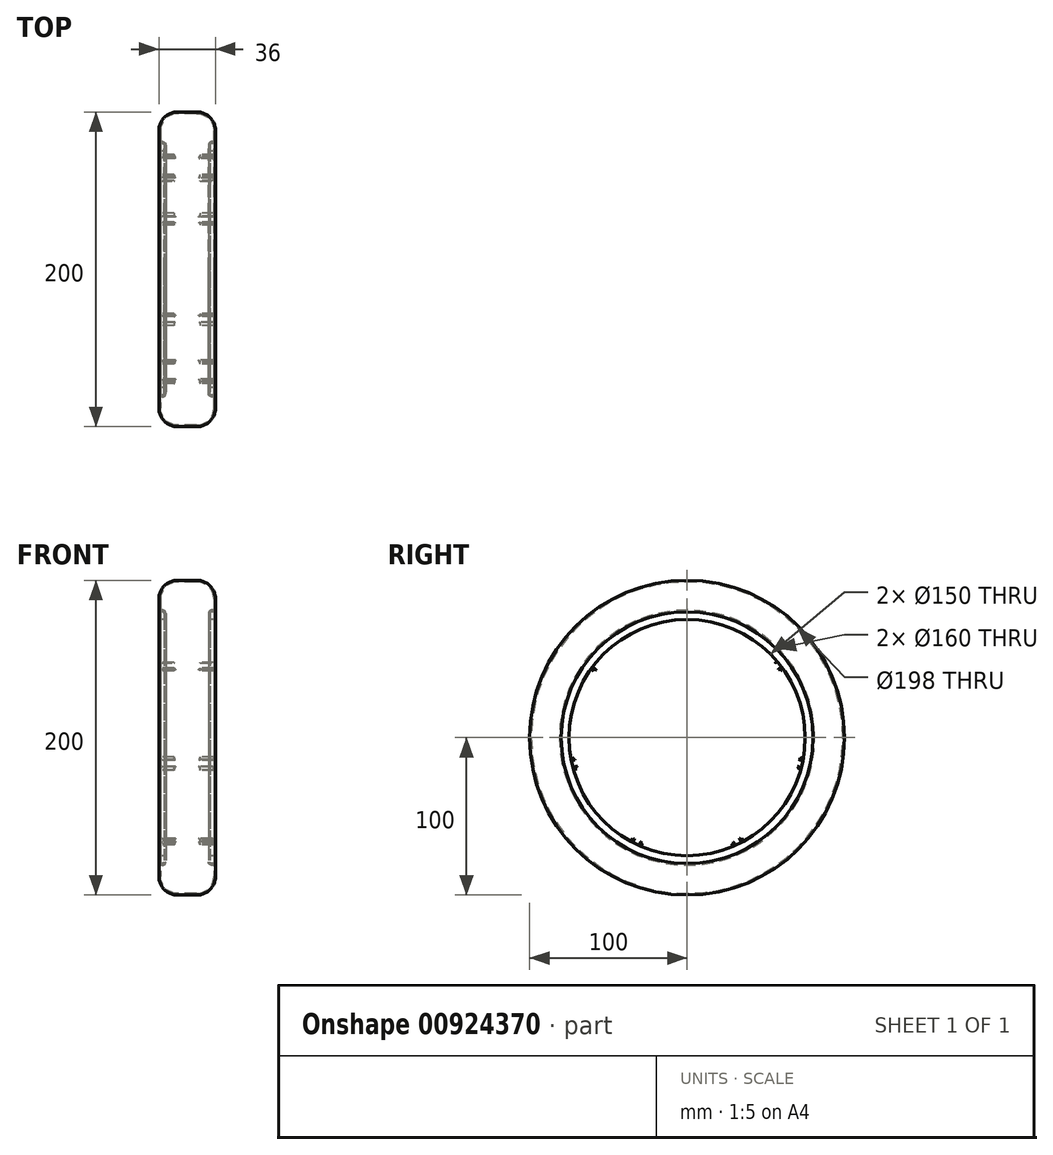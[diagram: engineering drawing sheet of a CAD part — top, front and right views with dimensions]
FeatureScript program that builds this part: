
annotation { "Feature Type Name" : "Feature", "Feature Type Description" : "" }
export const myFeature = defineFeature(function(context is Context, id is Id, definition is map)
    precondition{}
    {
        {
            var Q0;
            Q0=qCreatedBy(makeId("Front.planeOp"),FACE);
            var sketch = newSketch(context, id + "F0", { "sketchPlane" : qUnion([Q0])});
            skLineSegment(sketch, "E0", {"start": v(0, 0) * mm, "end": v(0, 100) * mm, "construction": true});
            skLineSegment(sketch, "E1", {"start": v(0, 5) * mm, "end": v(-17.27, 5) * mm});
            skLineSegment(sketch, "E2", {"start": v(0, 100) * mm, "end": v(-18, 100) * mm});
            skLineSegment(sketch, "E3", {"start": v(-18, 100) * mm, "end": v(-18, 80) * mm});
            skLineSegment(sketch, "E4", {"start": v(-17, 80) * mm, "end": v(-15.56, 80) * mm});
            skLineSegment(sketch, "E5", {"start": v(-8.99, 10) * mm, "end": v(0, 10) * mm});
            skLineSegment(sketch, "E6", {"start": v(-18, 79) * mm, "end": v(-18, 76.6) * mm});
            skLineSegment(sketch, "E7", {"start": v(-13.56, 75) * mm, "end": v(0, 75) * mm});
            skArc(sketch, "E8", {"start": v(-12.94, 18.39) * mm, "mid": v(-7.53, 46.64) * mm, "end": v(-17.11, 73.75) * mm});
            skLineSegment(sketch, "E9", {"start": v(-18, 80) * mm, "end": v(-14.56, 80) * mm});
            skLineSegment(sketch, "E10", {"start": v(-14.56, 79) * mm, "end": v(-14.56, 76) * mm});
            skPoint(sketch, "E11.visualSharp", {"position": v(-18, 80) * mm});
            skArc(sketch, "E11.filletArc", {"start": v(-17, 80) * mm, "mid": v(-17.7, 79.7) * mm, "end": v(-18, 79) * mm});
            skPoint(sketch, "E12.visualSharp", {"position": v(-14.56, 80) * mm});
            skArc(sketch, "E12.filletArc", {"start": v(-14.56, 79) * mm, "mid": v(-14.85, 79.7) * mm, "end": v(-15.56, 80) * mm});
            skPoint(sketch, "E13.visualSharp", {"position": v(-14.56, 75) * mm});
            skArc(sketch, "E13.filletArc", {"start": v(-14.56, 76) * mm, "mid": v(-14.26, 75.3) * mm, "end": v(-13.56, 75) * mm});
            skPoint(sketch, "E14.visualSharp", {"position": v(-18, 75) * mm});
            skArc(sketch, "E14.filletArc", {"start": v(-18, 76.6) * mm, "mid": v(-17.77, 75.1) * mm, "end": v(-17.11, 73.75) * mm});
            skArc(sketch, "E15.0", {"start": v(-8.99, 10) * mm, "mid": v(-2.77, 23.7) * mm, "end": v(0, 38.48) * mm});
            skArc(sketch, "E16.MirrorCS", {"start": v(8.99, 10) * mm, "mid": v(2.77, 23.7) * mm, "end": v(0, 38.48) * mm});
            skLineSegment(sketch, "E17.MirrorCS", {"start": v(13.56, 75) * mm, "end": v(0, 75) * mm});
            skLineSegment(sketch, "E18.MirrorCS", {"start": v(14.56, 79) * mm, "end": v(14.56, 76) * mm});
            skArc(sketch, "E19.MirrorCS", {"start": v(14.56, 76) * mm, "mid": v(14.26, 75.3) * mm, "end": v(13.56, 75) * mm});
            skLineSegment(sketch, "E20.MirrorCS", {"start": v(18, 80) * mm, "end": v(14.56, 80) * mm});
            skPoint(sketch, "E21.MirrorP", {"position": v(14.56, 80) * mm});
            skArc(sketch, "E22.MirrorCS", {"start": v(14.56, 79) * mm, "mid": v(14.85, 79.7) * mm, "end": v(15.56, 80) * mm});
            skArc(sketch, "E23.MirrorCS", {"start": v(17, 80) * mm, "mid": v(17.7, 79.7) * mm, "end": v(18, 79) * mm});
            skLineSegment(sketch, "E24.MirrorCS", {"start": v(18, 79) * mm, "end": v(18, 76.6) * mm});
            skArc(sketch, "E25.MirrorCS", {"start": v(18, 76.6) * mm, "mid": v(17.77, 75.1) * mm, "end": v(17.11, 73.75) * mm});
            skArc(sketch, "E26.MirrorCS", {"start": v(12.45, 19.4) * mm, "mid": v(7.57, 47.2) * mm, "end": v(17.11, 73.75) * mm});
            skLineSegment(sketch, "E27.MirrorCS", {"start": v(8.99, 10) * mm, "end": v(0, 10) * mm});
            skLineSegment(sketch, "E28.MirrorCS", {"start": v(0, 5) * mm, "end": v(17.02, 5) * mm});
            skPoint(sketch, "E29.orphan", {"position": v(18, 10) * mm});
            skPoint(sketch, "E30.visualSharp", {"position": v(-18, 10) * mm});
            skArc(sketch, "E30.filletArc", {"start": v(-12.94, 18.39) * mm, "mid": v(-15.58, 11.85) * mm, "end": v(-17.27, 5) * mm});
            skArc(sketch, "E31.filletArc", {"start": v(17.02, 5) * mm, "mid": v(15.2, 12.35) * mm, "end": v(12.45, 19.4) * mm});
            skPoint(sketch, "E32.MirrorCS.start.orphan", {"position": v(18, 5) * mm});
            skPoint(sketch, "E33.orphan", {"position": v(-18, 5) * mm});
            skLineSegment(sketch, "E34", {"start": v(0, 0) * mm, "end": v(32.12, 0) * mm, "construction": true});
            skArc(sketch, "E35.trimOffspring", {"start": v(0, 46.52) * mm, "mid": v(-2.55, 60.61) * mm, "end": v(-8.25, 73.76) * mm});
            skArc(sketch, "E36.trimOffspring", {"start": v(0, 46.52) * mm, "mid": v(2.55, 60.61) * mm, "end": v(8.25, 73.76) * mm});
            skLineSegment(sketch, "E37", {"start": v(-8.25, 73.76) * mm, "end": v(8.25, 73.76) * mm});
            skPoint(sketch, "E38.orphan", {"position": v(7.27, 72) * mm});
            skPoint(sketch, "E39.end.orphan", {"position": v(0, 72) * mm});
            skPoint(sketch, "E39.start.orphan", {"position": v(-7.27, 72) * mm});
            skSolve(sketch);
        }
        {
            var Q0;
            Q0=makeQuery(id+"F0.imprint","IMPRINT",FACE,{"disambiguationData":[TD([[makeQuery(id+"F0.imprint","IMPRINT",EDGE,{"derivedFrom":sQuery(id+"F0.wireOp",EDGE,"E1")}),-1.0]])]});
            var Q1;
            Q1=sQuery(id+"F0.wireOp",EDGE,"E34");
            revolve(context, id + "F1", {"surfaceOperationType" : NewSurfaceOperationType.NEW, "entities" : qUnion([Q0]), "axis" : qUnion([Q1]), "revolveType" : RevolveType.FULL});
        }
        {
            var Q0;
            Q0=qCreatedBy(makeId("Right.planeOp"),FACE);
            var sketch = newSketch(context, id + "F2", { "sketchPlane" : qUnion([Q0])});
            skArc(sketch, "E40.0", {"start": v(-56.3, 47.63) * mm, "mid": v(-32, 66.45) * mm, "end": v(-2.13, 73.72) * mm});
            skArc(sketch, "E41.0", {"start": v(16.09, -10.85) * mm, "mid": v(15.17, -12.1) * mm, "end": v(14.16, -13.27) * mm});
            skCircle(sketch, "E42.0", {"center": v(0, 0) * mm, "radius": 75 * mm});
            skLineSegment(sketch, "E43", {"start": v(-2.13, 73.72) * mm, "end": v(-7, 18.1) * mm});
            skLineSegment(sketch, "E44.MirrorCS", {"start": v(2.13, 73.72) * mm, "end": v(7, 18.1) * mm});
            skLineSegment(sketch, "E45.1.0", {"start": v(-58.97, 44.3) * mm, "end": v(-18.51, 5.81) * mm});
            skLineSegment(sketch, "E45.1.1", {"start": v(-56.3, 47.63) * mm, "end": v(-9.79, 16.76) * mm});
            skLineSegment(sketch, "E45.2.0", {"start": v(-71.4, -18.49) * mm, "end": v(-16.09, -10.85) * mm});
            skLineSegment(sketch, "E45.2.1", {"start": v(-72.35, -14.33) * mm, "end": v(-19.2, 2.8) * mm});
            skLineSegment(sketch, "E45.3.0", {"start": v(-30.07, -67.35) * mm, "end": v(-1.55, -19.34) * mm});
            skLineSegment(sketch, "E45.3.1", {"start": v(-33.9, -65.5) * mm, "end": v(-14.16, -13.27) * mm});
            skLineSegment(sketch, "E45.4.0", {"start": v(33.9, -65.5) * mm, "end": v(14.16, -13.27) * mm});
            skLineSegment(sketch, "E45.4.1", {"start": v(30.07, -67.35) * mm, "end": v(1.55, -19.34) * mm});
            skLineSegment(sketch, "E45.5.0", {"start": v(72.35, -14.33) * mm, "end": v(19.2, 2.8) * mm});
            skLineSegment(sketch, "E45.5.1", {"start": v(71.4, -18.49) * mm, "end": v(16.09, -10.85) * mm});
            skLineSegment(sketch, "E45.6.0", {"start": v(56.3, 47.63) * mm, "end": v(9.79, 16.76) * mm});
            skLineSegment(sketch, "E45.6.1", {"start": v(58.97, 44.3) * mm, "end": v(18.51, 5.81) * mm});
            skArc(sketch, "E46.trimOffspring", {"start": v(2.13, 73.72) * mm, "mid": v(32, 66.45) * mm, "end": v(56.3, 47.63) * mm});
            skArc(sketch, "E47.trimOffspring", {"start": v(58.97, 44.3) * mm, "mid": v(71.9, 16.41) * mm, "end": v(72.35, -14.33) * mm});
            skArc(sketch, "E48.trimOffspring", {"start": v(71.4, -18.49) * mm, "mid": v(57.66, -45.99) * mm, "end": v(33.9, -65.5) * mm});
            skArc(sketch, "E49.trimOffspring", {"start": v(-9.79, 16.76) * mm, "mid": v(-8.42, 17.48) * mm, "end": v(-7, 18.1) * mm});
            skArc(sketch, "E50.trimOffspring", {"start": v(7, 18.1) * mm, "mid": v(8.42, 17.48) * mm, "end": v(9.79, 16.76) * mm});
            skArc(sketch, "E51.trimOffspring", {"start": v(18.51, 5.81) * mm, "mid": v(18.92, 4.32) * mm, "end": v(19.2, 2.8) * mm});
            skArc(sketch, "E52.trimOffspring", {"start": v(1.55, -19.34) * mm, "mid": v(0, -19.4) * mm, "end": v(-1.55, -19.34) * mm});
            skArc(sketch, "E53.trimOffspring", {"start": v(-14.16, -13.27) * mm, "mid": v(-15.17, -12.1) * mm, "end": v(-16.09, -10.85) * mm});
            skArc(sketch, "E54.trimOffspring", {"start": v(-19.2, 2.8) * mm, "mid": v(-18.92, 4.32) * mm, "end": v(-18.51, 5.81) * mm});
            skArc(sketch, "E55.trimOffspring", {"start": v(-72.35, -14.33) * mm, "mid": v(-71.9, 16.41) * mm, "end": v(-58.97, 44.3) * mm});
            skArc(sketch, "E56.trimOffspring", {"start": v(-33.9, -65.5) * mm, "mid": v(-57.66, -45.99) * mm, "end": v(-71.4, -18.49) * mm});
            skArc(sketch, "E57.trimOffspring", {"start": v(30.07, -67.35) * mm, "mid": v(0, -73.75) * mm, "end": v(-30.07, -67.35) * mm});
            skSolve(sketch);
        }
        {
            var Q0;
            Q0=qCreatedBy(makeId("Right.planeOp"),FACE);
            var sketch = newSketch(context, id + "F3", { "sketchPlane" : qUnion([Q0])});
            skArc(sketch, "E58.0", {"start": v(2.13, 73.72) * mm, "mid": v(32, 66.45) * mm, "end": v(56.3, 47.63) * mm});
            skLineSegment(sketch, "E59", {"start": v(0, 38.48) * mm, "end": v(0, 10) * mm});
            skCircle(sketch, "E60", {"center": v(0, 0) * mm, "radius": 10 * mm});
            skLineSegment(sketch, "E61", {"start": v(2.13, 73.72) * mm, "end": v(3.86, 9.23) * mm});
            skLineSegment(sketch, "E62.MirrorCS", {"start": v(-2.13, 73.72) * mm, "end": v(-3.86, 9.23) * mm});
            skArc(sketch, "E63.0", {"start": v(-56.37, 47.56) * mm, "mid": v(-32.04, 66.43) * mm, "end": v(-2.13, 73.72) * mm});
            skArc(sketch, "E64.0", {"start": v(-72.35, -14.33) * mm, "mid": v(-71.9, 16.41) * mm, "end": v(-58.97, 44.3) * mm});
            skArc(sketch, "E65.0", {"start": v(-33.9, -65.5) * mm, "mid": v(-57.66, -45.99) * mm, "end": v(-71.4, -18.49) * mm});
            skArc(sketch, "E66.0", {"start": v(30.07, -67.35) * mm, "mid": v(0, -73.75) * mm, "end": v(-30.07, -67.35) * mm});
            skArc(sketch, "E67.0", {"start": v(71.4, -18.49) * mm, "mid": v(57.66, -45.99) * mm, "end": v(33.9, -65.5) * mm});
            skArc(sketch, "E68.0", {"start": v(58.97, 44.3) * mm, "mid": v(71.9, 16.41) * mm, "end": v(72.35, -14.33) * mm});
            skLineSegment(sketch, "E69.1.0", {"start": v(56.3, 47.65) * mm, "end": v(4.8, 8.77) * mm});
            skLineSegment(sketch, "E69.1.1", {"start": v(58.96, 44.31) * mm, "end": v(9.62, 2.74) * mm});
            skLineSegment(sketch, "E69.2.0", {"start": v(72.36, -14.3) * mm, "end": v(9.85, 1.7) * mm});
            skLineSegment(sketch, "E69.2.1", {"start": v(71.4, -18.46) * mm, "end": v(8.14, -5.8) * mm});
            skLineSegment(sketch, "E69.3.0", {"start": v(33.95, -65.48) * mm, "end": v(7.48, -6.64) * mm});
            skLineSegment(sketch, "E69.3.1", {"start": v(30.1, -67.33) * mm, "end": v(0.54, -9.99) * mm});
            skLineSegment(sketch, "E69.4.0", {"start": v(-30, -67.37) * mm, "end": v(-0.52, -9.99) * mm});
            skLineSegment(sketch, "E69.4.1", {"start": v(-33.86, -65.53) * mm, "end": v(-7.47, -6.65) * mm});
            skLineSegment(sketch, "E69.5.0", {"start": v(-71.38, -18.56) * mm, "end": v(-8.13, -5.82) * mm});
            skLineSegment(sketch, "E69.5.1", {"start": v(-72.34, -14.4) * mm, "end": v(-9.86, 1.7) * mm});
            skLineSegment(sketch, "E69.6.0", {"start": v(-59.03, 44.22) * mm, "end": v(-9.62, 2.73) * mm});
            skLineSegment(sketch, "E69.6.1", {"start": v(-56.37, 47.56) * mm, "end": v(-4.82, 8.76) * mm});
            skLineSegment(sketch, "E69.anchor1", {"start": v(0, 0) * mm, "end": v(-3.86, 9.23) * mm, "construction": true});
            skLineSegment(sketch, "E69.anchor2", {"start": v(0, 0) * mm, "end": v(-9.62, 2.73) * mm, "construction": true});
            skPoint(sketch, "E70.newPointA", {"position": v(-56.37, 47.56) * mm});
            skPoint(sketch, "E70.newPointB", {"position": v(-56.3, 47.63) * mm});
            skSolve(sketch);
        }
        {
            var Q0;
            Q0=qCreatedBy(makeId("Right.planeOp"),FACE);
            var sketch = newSketch(context, id + "F4", { "sketchPlane" : qUnion([Q0])});
            skCircle(sketch, "E71.0", {"center": v(0, 0) * mm, "radius": 10 * mm});
            skLineSegment(sketch, "E72.0", {"start": v(-54.65, 46.27) * mm, "end": v(-5.9, 9.58) * mm});
            skLineSegment(sketch, "E73.0", {"start": v(-2.2, 71.58) * mm, "end": v(-3.82, 10.58) * mm});
            skArc(sketch, "E74.0", {"start": v(-54.94, 49.2) * mm, "mid": v(-32.04, 66.43) * mm, "end": v(-4.3, 73.63) * mm});
            skPoint(sketch, "E75.visualSharp", {"position": v(-56.37, 47.56) * mm});
            skArc(sketch, "E75.filletArc", {"start": v(-54.94, 49.2) * mm, "mid": v(-55.44, 47.68) * mm, "end": v(-54.65, 46.27) * mm});
            skPoint(sketch, "E76.visualSharp", {"position": v(-2.13, 73.72) * mm});
            skArc(sketch, "E76.filletArc", {"start": v(-2.2, 71.58) * mm, "mid": v(-2.8, 73.07) * mm, "end": v(-4.3, 73.63) * mm});
            skArc(sketch, "E77", {"start": v(-5.9, 9.58) * mm, "mid": v(-4.56, 9.45) * mm, "end": v(-3.82, 10.58) * mm});
            skPoint(sketch, "E78.orphan", {"position": v(-4.82, 8.76) * mm});
            skPoint(sketch, "E79.orphan", {"position": v(-3.86, 9.23) * mm});
            skLineSegment(sketch, "E80.1.0", {"start": v(2.09, 71.58) * mm, "end": v(3.8, 10.59) * mm});
            skArc(sketch, "E80.1.1", {"start": v(3.8, 10.59) * mm, "mid": v(4.54, 9.45) * mm, "end": v(5.9, 9.59) * mm});
            skLineSegment(sketch, "E80.1.2", {"start": v(54.59, 46.35) * mm, "end": v(5.9, 9.59) * mm});
            skArc(sketch, "E80.1.3", {"start": v(4.2, 73.64) * mm, "mid": v(31.95, 66.48) * mm, "end": v(54.87, 49.29) * mm});
            skArc(sketch, "E80.1.4", {"start": v(54.59, 46.35) * mm, "mid": v(55.37, 47.76) * mm, "end": v(54.87, 49.29) * mm});
            skArc(sketch, "E80.1.5", {"start": v(4.2, 73.64) * mm, "mid": v(2.7, 73.07) * mm, "end": v(2.09, 71.58) * mm});
            skLineSegment(sketch, "E80.2.0", {"start": v(57.26, 43.01) * mm, "end": v(10.65, 3.63) * mm});
            skArc(sketch, "E80.2.1", {"start": v(10.65, 3.63) * mm, "mid": v(10.22, 2.34) * mm, "end": v(11.17, 1.37) * mm});
            skLineSegment(sketch, "E80.2.2", {"start": v(70.28, -13.76) * mm, "end": v(11.17, 1.37) * mm});
            skArc(sketch, "E80.2.3", {"start": v(60.18, 42.64) * mm, "mid": v(71.89, 16.49) * mm, "end": v(72.75, -12.15) * mm});
            skArc(sketch, "E80.2.4", {"start": v(70.28, -13.76) * mm, "mid": v(71.87, -13.5) * mm, "end": v(72.75, -12.15) * mm});
            skArc(sketch, "E80.2.5", {"start": v(60.18, 42.64) * mm, "mid": v(58.8, 43.47) * mm, "end": v(57.26, 43.01) * mm});
            skLineSegment(sketch, "E80.3.0", {"start": v(69.33, -17.93) * mm, "end": v(9.48, -6.06) * mm});
            skArc(sketch, "E80.3.1", {"start": v(9.48, -6.06) * mm, "mid": v(8.2, -6.53) * mm, "end": v(8.04, -7.87) * mm});
            skLineSegment(sketch, "E80.3.2", {"start": v(33.07, -63.52) * mm, "end": v(8.04, -7.87) * mm});
            skArc(sketch, "E80.3.3", {"start": v(70.86, -20.45) * mm, "mid": v(57.72, -45.91) * mm, "end": v(35.87, -64.45) * mm});
            skArc(sketch, "E80.3.4", {"start": v(33.07, -63.52) * mm, "mid": v(34.26, -64.6) * mm, "end": v(35.87, -64.45) * mm});
            skArc(sketch, "E80.3.5", {"start": v(70.86, -20.45) * mm, "mid": v(70.65, -18.86) * mm, "end": v(69.33, -17.93) * mm});
            skLineSegment(sketch, "E80.4.0", {"start": v(29.22, -65.38) * mm, "end": v(1.17, -11.2) * mm});
            skArc(sketch, "E80.4.1", {"start": v(1.17, -11.2) * mm, "mid": v(0.02, -10.49) * mm, "end": v(-1.14, -11.2) * mm});
            skLineSegment(sketch, "E80.4.2", {"start": v(-29.03, -65.47) * mm, "end": v(-1.14, -11.2) * mm});
            skArc(sketch, "E80.4.3", {"start": v(28.2, -68.15) * mm, "mid": v(0.1, -73.75) * mm, "end": v(-28, -68.23) * mm});
            skArc(sketch, "E80.4.4", {"start": v(-29.03, -65.47) * mm, "mid": v(-29.13, -67.07) * mm, "end": v(-28, -68.23) * mm});
            skArc(sketch, "E80.4.5", {"start": v(28.2, -68.15) * mm, "mid": v(29.32, -66.99) * mm, "end": v(29.22, -65.38) * mm});
            skLineSegment(sketch, "E80.5.0", {"start": v(-32.89, -63.62) * mm, "end": v(-8.02, -7.9) * mm});
            skArc(sketch, "E80.5.1", {"start": v(-8.02, -7.9) * mm, "mid": v(-8.19, -6.55) * mm, "end": v(-9.46, -6.09) * mm});
            skLineSegment(sketch, "E80.5.2", {"start": v(-69.28, -18.14) * mm, "end": v(-9.46, -6.09) * mm});
            skArc(sketch, "E80.5.3", {"start": v(-35.68, -64.55) * mm, "mid": v(-57.59, -46.08) * mm, "end": v(-70.8, -20.66) * mm});
            skArc(sketch, "E80.5.4", {"start": v(-69.28, -18.14) * mm, "mid": v(-70.6, -19.06) * mm, "end": v(-70.8, -20.66) * mm});
            skArc(sketch, "E80.5.5", {"start": v(-35.68, -64.55) * mm, "mid": v(-34.08, -64.7) * mm, "end": v(-32.89, -63.62) * mm});
            skLineSegment(sketch, "E80.6.0", {"start": v(-70.24, -13.97) * mm, "end": v(-11.17, 1.34) * mm});
            skArc(sketch, "E80.6.1", {"start": v(-11.17, 1.34) * mm, "mid": v(-10.23, 2.31) * mm, "end": v(-10.66, 3.6) * mm});
            skLineSegment(sketch, "E80.6.2", {"start": v(-57.38, 42.84) * mm, "end": v(-10.66, 3.6) * mm});
            skArc(sketch, "E80.6.3", {"start": v(-72.71, -12.37) * mm, "mid": v(-71.94, 16.28) * mm, "end": v(-60.3, 42.46) * mm});
            skArc(sketch, "E80.6.4", {"start": v(-57.38, 42.84) * mm, "mid": v(-58.93, 43.3) * mm, "end": v(-60.3, 42.46) * mm});
            skArc(sketch, "E80.6.5", {"start": v(-72.71, -12.37) * mm, "mid": v(-71.83, -13.71) * mm, "end": v(-70.24, -13.97) * mm});
            skLineSegment(sketch, "E80.anchor1", {"start": v(0, 0) * mm, "end": v(-54.65, 46.27) * mm, "construction": true});
            skLineSegment(sketch, "E80.anchor2", {"start": v(0, 0) * mm, "end": v(-70.24, -13.97) * mm, "construction": true});
            skSolve(sketch);
        }
        {
            var Q0;
            Q0=makeQuery(id+"F4.imprint","IMPRINT",FACE,{"disambiguationData":[TD([[makeQuery(id+"F4.imprint","IMPRINT",EDGE,{"derivedFrom":sQuery(id+"F4.wireOp",EDGE,"E80.6.0")}),1.0]])]});
            var Q1;
            Q1=makeQuery(id+"F2.imprint","IMPRINT",FACE,{"disambiguationData":[TD([[makeQuery(id+"F2.imprint","IMPRINT",EDGE,{"derivedFrom":sQuery(id+"F2.wireOp",EDGE,"E40.0")}),-1.0]])]});
            var Q2;
            {var subQ0=sQuery(id+"F3.wireOp",EDGE,"E62.MirrorCS");Q2=makeQuery(id+"F3.imprint","IMPRINT",FACE,{"disambiguationData":[TD([[makeQuery(id+"F3.imprint","IMPRINT",EDGE,{"derivedFrom":subQ0}),-1.0]])]});}
            var Q3;
            {var subQ0=sQuery(id+"F3.wireOp",EDGE,"E61");Q3=makeQuery(id+"F3.imprint","IMPRINT",FACE,{"disambiguationData":[TD([[makeQuery(id+"F3.imprint","IMPRINT",EDGE,{"derivedFrom":subQ0}),1.0]])]});}
            var Q4;
            Q4=makeQuery(id+"F4.imprint","IMPRINT",FACE,{"disambiguationData":[TD([[makeQuery(id+"F4.imprint","IMPRINT",EDGE,{"derivedFrom":sQuery(id+"F4.wireOp",EDGE,"E80.2.0")}),1.0]])]});
            var Q5;
            Q5=makeQuery(id+"F4.imprint","IMPRINT",FACE,{"disambiguationData":[TD([[makeQuery(id+"F4.imprint","IMPRINT",EDGE,{"derivedFrom":sQuery(id+"F4.wireOp",EDGE,"E80.3.0")}),1.0]])]});
            var Q6;
            Q6=makeQuery(id+"F4.imprint","IMPRINT",FACE,{"disambiguationData":[TD([[makeQuery(id+"F4.imprint","IMPRINT",EDGE,{"derivedFrom":sQuery(id+"F4.wireOp",EDGE,"E80.4.0")}),1.0]])]});
            var Q7;
            Q7=makeQuery(id+"F4.imprint","IMPRINT",FACE,{"disambiguationData":[TD([[makeQuery(id+"F4.imprint","IMPRINT",EDGE,{"derivedFrom":sQuery(id+"F4.wireOp",EDGE,"E80.5.0")}),1.0]])]});
            extrude(context, id + "F5", {"entities" : qUnion([Q0, Q1, Q2, Q3, Q4, Q5, Q6, Q7]), "operationType" : NewBodyOperationType.REMOVE, "endBound" : BoundingType.SYMMETRIC, "depth" : 100 * mm, "offsetDistance" : 25 * mm});
        }
        {
            var Q0;
            Q0=qCreatedBy(makeId("Front.planeOp"),FACE);
            var sketch = newSketch(context, id + "F6", { "sketchPlane" : qUnion([Q0])});
            skLineSegment(sketch, "E81.0", {"start": v(-14.56, 79) * mm, "end": v(-14.56, 76) * mm});
            skArc(sketch, "E82.0", {"start": v(-14.56, 79) * mm, "mid": v(-14.85, 79.7) * mm, "end": v(-15.56, 80) * mm});
            skLineSegment(sketch, "E83.0", {"start": v(-17, 80) * mm, "end": v(-15.56, 80) * mm});
            skArc(sketch, "E84.0", {"start": v(-14.56, 76) * mm, "mid": v(-14.26, 75.3) * mm, "end": v(-13.56, 75) * mm});
            skLineSegment(sketch, "E85.0", {"start": v(-13.56, 75) * mm, "end": v(0, 75) * mm});
            skLineSegment(sketch, "E86.0", {"start": v(13.56, 75) * mm, "end": v(0, 75) * mm});
            skArc(sketch, "E87.0", {"start": v(14.56, 76) * mm, "mid": v(14.26, 75.3) * mm, "end": v(13.56, 75) * mm});
            skLineSegment(sketch, "E88.0", {"start": v(14.56, 79) * mm, "end": v(14.56, 76) * mm});
            skArc(sketch, "E89.0", {"start": v(14.56, 79) * mm, "mid": v(14.85, 79.7) * mm, "end": v(15.56, 80) * mm});
            skLineSegment(sketch, "E90.0", {"start": v(17, 80) * mm, "end": v(15.56, 80) * mm});
            skArc(sketch, "E91.MirrorCS", {"start": v(17, 80) * mm, "mid": v(17.7, 80.3) * mm, "end": v(18, 81) * mm});
            skArc(sketch, "E92.MirrorCS", {"start": v(-17, 80) * mm, "mid": v(-17.7, 80.3) * mm, "end": v(-18, 81) * mm});
            skPoint(sketch, "E93.orphan", {"position": v(-18, 80) * mm});
            skPoint(sketch, "E94.0.end.orphan", {"position": v(-18, 79) * mm});
            skPoint(sketch, "E94.0.start.orphan", {"position": v(-17, 80) * mm});
            skPoint(sketch, "E95.orphan", {"position": v(-14.56, 80) * mm});
            skPoint(sketch, "E96.orphan", {"position": v(14.56, 80) * mm});
            skPoint(sketch, "E97.0.end.orphan", {"position": v(18, 79) * mm});
            skPoint(sketch, "E97.0.start.orphan", {"position": v(17, 80) * mm});
            skPoint(sketch, "E98.orphan", {"position": v(18, 80) * mm});
            skLineSegment(sketch, "E99.0", {"start": v(0, 100) * mm, "end": v(-6, 100) * mm});
            skLineSegment(sketch, "E100", {"start": v(-18, 88) * mm, "end": v(-18, 81) * mm});
            skPoint(sketch, "E101.visualSharp", {"position": v(-18, 100) * mm});
            skArc(sketch, "E101.filletArc", {"start": v(-6, 100) * mm, "mid": v(-14.49, 96.49) * mm, "end": v(-18, 88) * mm});
            skArc(sketch, "E102.MirrorCS", {"start": v(6, 100) * mm, "mid": v(14.49, 96.49) * mm, "end": v(18, 88) * mm});
            skLineSegment(sketch, "E103.MirrorCS", {"start": v(0, 100) * mm, "end": v(6, 100) * mm});
            skLineSegment(sketch, "E104.MirrorCS", {"start": v(18, 88) * mm, "end": v(18, 81) * mm});
            skLineSegment(sketch, "E105.0", {"start": v(-17, 88) * mm, "end": v(-17, 81.23) * mm});
            skArc(sketch, "E105.1", {"start": v(-6, 99) * mm, "mid": v(-13.78, 95.78) * mm, "end": v(-17, 88) * mm});
            skLineSegment(sketch, "E105.2", {"start": v(17, 88) * mm, "end": v(17, 81) * mm});
            skArc(sketch, "E105.3", {"start": v(6, 99) * mm, "mid": v(13.78, 95.78) * mm, "end": v(17, 88) * mm});
            skLineSegment(sketch, "E105.4", {"start": v(0, 99) * mm, "end": v(6, 99) * mm});
            skLineSegment(sketch, "E105.5", {"start": v(0, 99) * mm, "end": v(-6, 99) * mm});
            skLineSegment(sketch, "E106.0", {"start": v(-13.56, 79) * mm, "end": v(-13.56, 75) * mm});
            skArc(sketch, "E106.1", {"start": v(-13.56, 79) * mm, "mid": v(-14.14, 80.41) * mm, "end": v(-15.56, 81) * mm});
            skLineSegment(sketch, "E106.2", {"start": v(-16.77, 81) * mm, "end": v(-15.56, 81) * mm});
            skArc(sketch, "E107.filletArc", {"start": v(-17, 81.23) * mm, "mid": v(-16.93, 81.07) * mm, "end": v(-16.77, 81) * mm});
            skArc(sketch, "E108.MirrorCS", {"start": v(17, 81.23) * mm, "mid": v(16.93, 81.07) * mm, "end": v(16.77, 81) * mm});
            skLineSegment(sketch, "E109.MirrorCS", {"start": v(16.77, 81) * mm, "end": v(15.56, 81) * mm});
            skArc(sketch, "E110.MirrorCS", {"start": v(13.56, 79) * mm, "mid": v(14.14, 80.41) * mm, "end": v(15.56, 81) * mm});
            skLineSegment(sketch, "E111.MirrorCS", {"start": v(13.56, 79) * mm, "end": v(13.56, 75) * mm});
            skSolve(sketch);
        }
        {
            var Q0;
            Q0=makeQuery(id+"F6.imprint","IMPRINT",FACE,{"disambiguationData":[TD([[makeQuery(id+"F6.imprint","IMPRINT",EDGE,{"derivedFrom":sQuery(id+"F6.wireOp",EDGE,"E81.0")}),1.0]])]});
            var Q1;
            Q1=sQuery(id+"F0.wireOp",EDGE,"E34");
            revolve(context, id + "F7", {"surfaceOperationType" : NewSurfaceOperationType.NEW, "entities" : qUnion([Q0]), "axis" : qUnion([Q1]), "revolveType" : RevolveType.FULL});
        }
    });
